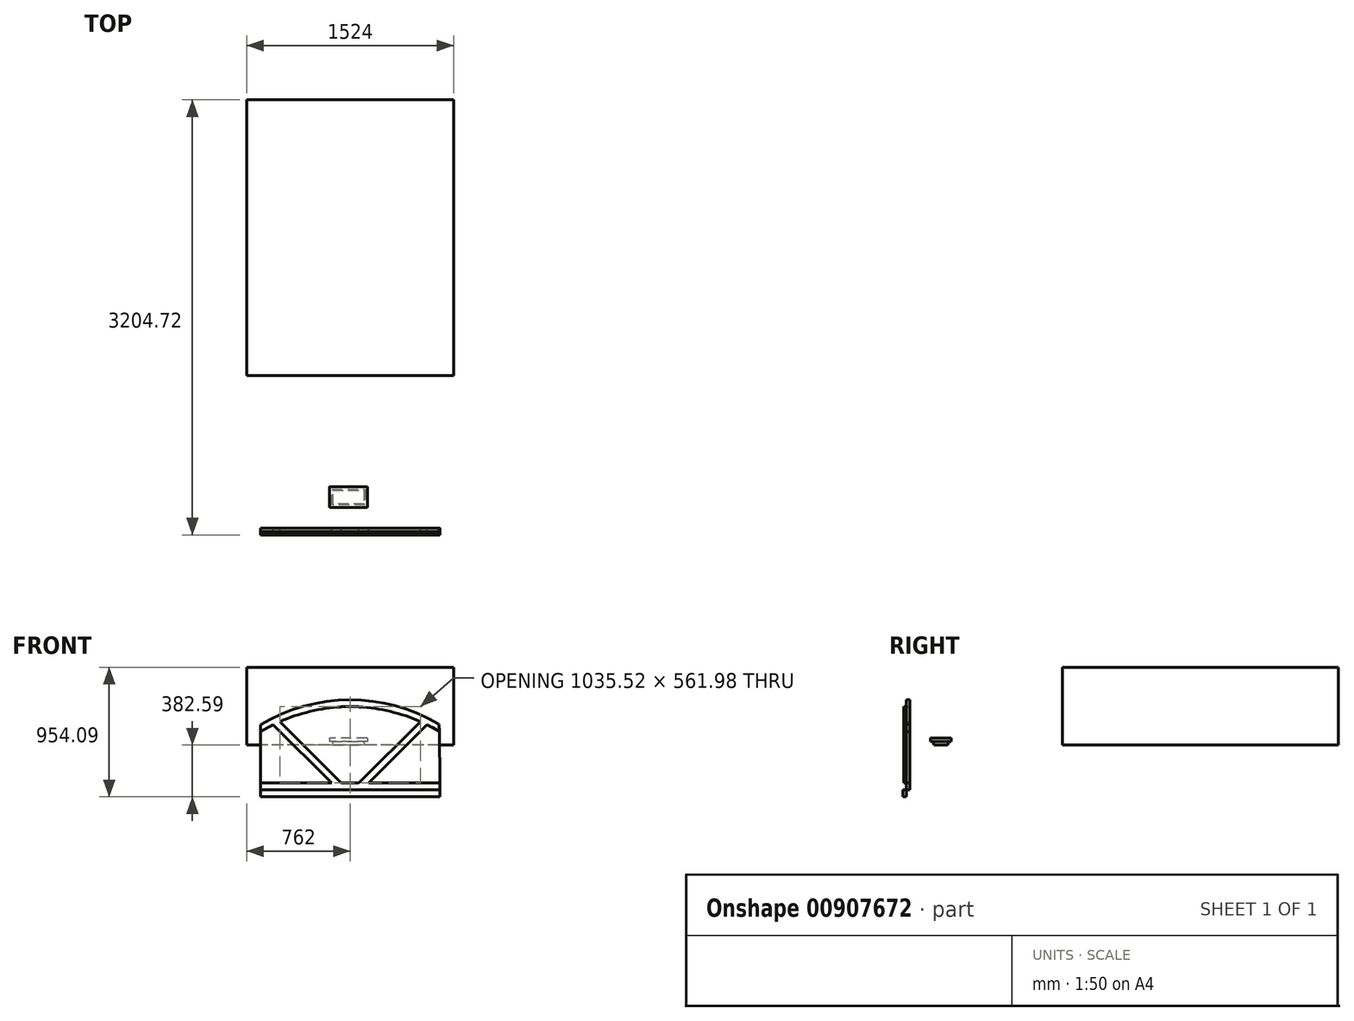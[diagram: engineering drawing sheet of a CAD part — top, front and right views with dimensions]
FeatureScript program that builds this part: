
annotation { "Feature Type Name" : "Feature", "Feature Type Description" : "" }
export const myFeature = defineFeature(function(context is Context, id is Id, definition is map)
    precondition{}
    {
        {
            var Q0;
            Q0=qCreatedBy(makeId("Front.planeOp"),FACE);
            var sketch = newSketch(context, id + "F0", { "sketchPlane" : qUnion([Q0])});
            skLineSegment(sketch, "E0.bottom", {"start": v(65.07, 331.79) * mm, "end": v(-65.07, 331.79) * mm});
            skLineSegment(sketch, "E0.top", {"start": v(660.4, -331.79) * mm, "end": v(-660.4, -331.79) * mm});
            skLineSegment(sketch, "E0.left", {"start": v(660.4, -280.99) * mm, "end": v(660.4, -331.79) * mm});
            skLineSegment(sketch, "E0.right", {"start": v(-660.4, 148.46) * mm, "end": v(-660.4, 97.66) * mm});
            skPoint(sketch, "E0.middle", {"position": v(0, 0) * mm});
            skLineSegment(sketch, "E1", {"start": v(92.3, -280.99) * mm, "end": v(660.4, -280.99) * mm});
            skLineSegment(sketch, "E2", {"start": v(660.4, -280.99) * mm, "end": v(-660.4, -280.99) * mm});
            skLineSegment(sketch, "E3.bottom", {"start": v(-660.4, -280.99) * mm, "end": v(-65.07, -280.99) * mm});
            skLineSegment(sketch, "E3.left", {"start": v(-660.4, 97.66) * mm, "end": v(-660.4, 148.46) * mm});
            skLineSegment(sketch, "E3.right", {"start": v(-65.07, 279.33) * mm, "end": v(-65.07, 280.99) * mm});
            skLineSegment(sketch, "E4.bottom", {"start": v(660.4, -280.99) * mm, "end": v(65.07, -280.99) * mm});
            skLineSegment(sketch, "E4.right", {"start": v(65.07, 279.33) * mm, "end": v(65.07, 280.99) * mm});
            skPoint(sketch, "E5.endSnap0", {"position": v(0, -331.79) * mm});
            skArc(sketch, "E6", {"start": v(660.4, -308.78) * mm, "mid": v(660.25, -294.88) * mm, "end": v(659.82, -280.99) * mm});
            skPoint(sketch, "E5.start.orphan", {"position": v(0, 331.79) * mm});
            skArc(sketch, "E7.trimOffspring", {"start": v(-659.82, -280.99) * mm, "mid": v(-660.22, -293.24) * mm, "end": v(-660.4, -305.5) * mm});
            skArc(sketch, "E8", {"start": v(0, 331.79) * mm, "mid": v(339.27, 286.05) * mm, "end": v(654.31, 152.1) * mm});
            skLineSegment(sketch, "E9", {"start": v(0, -949.34) * mm, "end": v(0, -1000.14) * mm});
            skLineSegment(sketch, "E10.bottom", {"start": v(65.07, 280.99) * mm, "end": v(-65.07, 280.99) * mm});
            skLineSegment(sketch, "E10.left", {"start": v(65.07, 330.13) * mm, "end": v(65.07, 331.79) * mm});
            skLineSegment(sketch, "E10.right", {"start": v(-65.07, 330.13) * mm, "end": v(-65.07, 331.79) * mm});
            skArc(sketch, "E11", {"start": v(0, 331.79) * mm, "mid": v(-342.69, 285.1) * mm, "end": v(-660.4, 148.46) * mm});
            skArc(sketch, "E12", {"start": v(0, 280.99) * mm, "mid": v(341, 234.77) * mm, "end": v(657.4, 99.46) * mm});
            skArc(sketch, "E13", {"start": v(0, 280.99) * mm, "mid": v(-342.69, 234.3) * mm, "end": v(-660.4, 97.66) * mm});
            skLineSegment(sketch, "E14", {"start": v(65.07, -280.99) * mm, "end": v(517.76, 171.7) * mm});
            skLineSegment(sketch, "E15", {"start": v(-65.07, -280.99) * mm, "end": v(-517.76, 171.7) * mm});
            skLineSegment(sketch, "E16", {"start": v(327.34, -90.56) * mm, "end": v(566.72, 148.82) * mm});
            skLineSegment(sketch, "E17", {"start": v(566.72, 148.82) * mm, "end": v(136.92, -280.99) * mm});
            skLineSegment(sketch, "E18", {"start": v(-327.34, -90.56) * mm, "end": v(-136.92, -280.99) * mm});
            skLineSegment(sketch, "E19", {"start": v(-136.92, -280.99) * mm, "end": v(-566.72, 148.82) * mm});
            skPoint(sketch, "E20.start.orphan", {"position": v(291.42, -54.64) * mm});
            skPoint(sketch, "E21.start.orphan", {"position": v(-291.42, -54.64) * mm});
            skPoint(sketch, "E22.orphan", {"position": v(65.07, 382.59) * mm});
            skPoint(sketch, "E23.orphan", {"position": v(-65.07, 382.59) * mm});
            skPoint(sketch, "E24.orphan", {"position": v(660.4, 331.79) * mm});
            skLineSegment(sketch, "E25.trimOffspring", {"start": v(-660.4, -280.99) * mm, "end": v(-660.4, -331.79) * mm});
            skPoint(sketch, "E26.orphan", {"position": v(-660.4, 331.79) * mm});
            skLineSegment(sketch, "E27", {"start": v(657.4, 99.46) * mm, "end": v(654.31, 152.1) * mm});
            skSolve(sketch);
        }
        {
            var Q0;
            {var subQ0=sQuery(id+"F0.wireOp",EDGE,"E15");Q0=makeQuery(id+"F0.imprint","IMPRINT",FACE,{"disambiguationData":[TD([[makeQuery(id+"F0.imprint","IMPRINT",EDGE,{"derivedFrom":subQ0}),1.0]])]});}
            var Q1;
            {var subQ9=sQuery(id+"F0.wireOp",EDGE,"E0.top");Q1=makeQuery(id+"F0.imprint","IMPRINT",FACE,{"disambiguationData":[TD([[makeQuery(id+"F0.imprint","IMPRINT",EDGE,{"derivedFrom":subQ9}),-1.0]])]});}
            var Q2;
            {var subQ0=sQuery(id+"F0.wireOp",EDGE,"E14");Q2=makeQuery(id+"F0.imprint","IMPRINT",FACE,{"disambiguationData":[TD([[makeQuery(id+"F0.imprint","IMPRINT",EDGE,{"derivedFrom":subQ0}),-1.0]])]});}
            var Q3;
            {var subQ8=sQuery(id+"F0.wireOp",EDGE,"E3.right");Q3=makeQuery(id+"F0.imprint","IMPRINT",FACE,{"disambiguationData":[TD([[makeQuery(id+"F0.imprint","IMPRINT",EDGE,{"derivedFrom":subQ8}),1.0]])]});}
            extrude(context, id + "F1", {"entities" : qUnion([Q0, Q1, Q2, Q3]), "depth" : 25.4 * mm, "offsetDistance" : 25.4 * mm});
        }
        {
            var Q0;
            Q0=makeQuery(id+"F1.opExtrude","CAP_FACE",FACE,{"disambiguationData":[OSD([sQuery(id+"F0.wireOp",EDGE,"E0.top"),sQuery(id+"F0.wireOp",EDGE,"E0.left"),sQuery(id+"F0.wireOp",EDGE,"E2"),sQuery(id+"F0.wireOp",EDGE,"E3.bottom"),sQuery(id+"F0.wireOp",EDGE,"E3.right"),sQuery(id+"F0.wireOp",EDGE,"E4.bottom"),sQuery(id+"F0.wireOp",EDGE,"E4.right"),sQuery(id+"F0.wireOp",EDGE,"E6"),sQuery(id+"F0.wireOp",EDGE,"E8"),sQuery(id+"F0.wireOp",EDGE,"E10.bottom"),sQuery(id+"F0.wireOp",EDGE,"E11"),sQuery(id+"F0.wireOp",EDGE,"E12"),sQuery(id+"F0.wireOp",EDGE,"E13"),sQuery(id+"F0.wireOp",EDGE,"E14"),sQuery(id+"F0.wireOp",EDGE,"E15"),sQuery(id+"F0.wireOp",EDGE,"E17"),sQuery(id+"F0.wireOp",EDGE,"E19"),sQuery(id+"F0.wireOp",EDGE,"E25.trimOffspring"),sQuery(id+"F0.wireOp",EDGE,"E0.right"),sQuery(id+"F0.wireOp",EDGE,"E27")])],"isStart":false});
            var sketch = newSketch(context, id + "F2", { "sketchPlane" : qUnion([Q0])});
            skLineSegment(sketch, "E28.bottom", {"start": v(-660.4, -331.79) * mm, "end": v(660.4, -331.79) * mm});
            skLineSegment(sketch, "E28.top", {"start": v(-660.4, -382.59) * mm, "end": v(660.4, -382.59) * mm});
            skLineSegment(sketch, "E28.left", {"start": v(-660.4, -331.79) * mm, "end": v(-660.4, -382.59) * mm});
            skLineSegment(sketch, "E28.right", {"start": v(660.4, -331.79) * mm, "end": v(660.4, -382.59) * mm});
            skSolve(sketch);
        }
        {
            var Q0;
            Q0=makeQuery(id+"F2.imprint","IMPRINT",FACE,{"disambiguationData":[TD([[makeQuery(id+"F2.imprint","IMPRINT",EDGE,{"derivedFrom":sQuery(id+"F2.wireOp",EDGE,"E28.bottom")}),1.0]])]});
            extrude(context, id + "F3", {"entities" : qUnion([Q0]), "depth" : 25.4 * mm, "offsetDistance" : 25.4 * mm});
        }
        {
            var Q0;
            Q0=qCreatedBy(makeId("Top.planeOp"),FACE);
            var sketch = newSketch(context, id + "F4", { "sketchPlane" : qUnion([Q0])});
            skLineSegment(sketch, "E29.bottom", {"start": v(101.76, 278.3) * mm, "end": v(-126.84, 278.3) * mm});
            skLineSegment(sketch, "E29.top", {"start": v(101.76, 176.7) * mm, "end": v(-126.84, 176.7) * mm});
            skLineSegment(sketch, "E29.left", {"start": v(101.76, 278.3) * mm, "end": v(101.76, 176.7) * mm});
            skLineSegment(sketch, "E29.right", {"start": v(-126.84, 278.3) * mm, "end": v(-126.84, 176.7) * mm});
            skPoint(sketch, "E29.middle", {"position": v(-12.54, 227.5) * mm});
            skSolve(sketch);
        }
        {
            var Q0;
            Q0=makeQuery(id+"F4.imprint","IMPRINT",FACE,{"disambiguationData":[TD([[makeQuery(id+"F4.imprint","IMPRINT",EDGE,{"derivedFrom":sQuery(id+"F4.wireOp",EDGE,"E29.bottom")}),1.0]])]});
            extrude(context, id + "F5", {"entities" : qUnion([Q0]), "depth" : 25.4 * mm, "offsetDistance" : 25.4 * mm, "hasDraft" : true, "draftAngle" : 15 * degree});
        }
        {
            var Q0;
            Q0=makeQuery(id+"F5.opExtrude","CAP_FACE",FACE,{"disambiguationData":[OSD([sQuery(id+"F4.wireOp",EDGE,"E29.bottom"),sQuery(id+"F4.wireOp",EDGE,"E29.top"),sQuery(id+"F4.wireOp",EDGE,"E29.left"),sQuery(id+"F4.wireOp",EDGE,"E29.right")])],"isStart":false});
            var sketch = newSketch(context, id + "F6", { "sketchPlane" : qUnion([Q0])});
            skLineSegment(sketch, "E30.bottom", {"start": v(127.16, 303.7) * mm, "end": v(-152.24, 303.7) * mm});
            skLineSegment(sketch, "E30.top", {"start": v(127.16, 151.3) * mm, "end": v(-152.24, 151.3) * mm});
            skLineSegment(sketch, "E30.left", {"start": v(127.16, 303.7) * mm, "end": v(127.16, 151.3) * mm});
            skLineSegment(sketch, "E30.right", {"start": v(-152.24, 303.7) * mm, "end": v(-152.24, 151.3) * mm});
            skPoint(sketch, "E30.middle", {"position": v(-12.54, 227.5) * mm});
            skPoint(sketch, "E30.middle.positionSnap0", {"position": v(-133.65, 227.5) * mm});
            skPoint(sketch, "E30.middle.positionSnap1", {"position": v(-12.54, 285.1) * mm});
            skPoint(sketch, "E30.centerSnap0", {"position": v(-133.65, 227.5) * mm});
            skPoint(sketch, "E30.centerSnap1", {"position": v(-12.54, 285.1) * mm});
            skSolve(sketch);
        }
        {
            var Q0;
            Q0=makeQuery(id+"F6.imprint","IMPRINT",FACE,{"disambiguationData":[TD([[makeQuery(id+"F6.imprint","IMPRINT",EDGE,{"derivedFrom":sQuery(id+"F6.wireOp",EDGE,"E30.bottom")}),1.0]])]});
            var Q1;
            Q1=makeQuery(id+"F6.imprint","IMPRINT",FACE,{"disambiguationData":[TD([[makeQuery(id+"F6.imprint","IMPRINT",EDGE,{"derivedFrom":makeQuery(id+"F5.opExtrude","CAP_EDGE",EDGE,{"disambiguationData":[OSD([sQuery(id+"F4.wireOp",EDGE,"E29.bottom")])],"isStart":false})}),1.0]])]});
            extrude(context, id + "F7", {"entities" : qUnion([Q0, Q1]), "operationType" : NewBodyOperationType.ADD, "depth" : 25.4 * mm, "offsetDistance" : 25.4 * mm});
        }
        {
            var Q0;
            Q0=makeQuery(id+"F7.opExtrude","CAP_EDGE",EDGE,{"disambiguationData":[OSD([sQuery(id+"F6.wireOp",EDGE,"E30.left")])],"isStart":false});
            var Q1;
            Q1=makeQuery(id+"F7.opExtrude","CAP_EDGE",EDGE,{"disambiguationData":[OSD([sQuery(id+"F6.wireOp",EDGE,"E30.top")])],"isStart":false});
            var Q2;
            Q2=makeQuery(id+"F7.opExtrude","CAP_EDGE",EDGE,{"disambiguationData":[OSD([sQuery(id+"F6.wireOp",EDGE,"E30.bottom")])],"isStart":false});
            var Q3;
            Q3=makeQuery(id+"F7.opExtrude","CAP_EDGE",EDGE,{"disambiguationData":[OSD([sQuery(id+"F6.wireOp",EDGE,"E30.right")])],"isStart":false});
            fillet(context, id + "F8", {"entities" : qUnion([Q0, Q1, Q2, Q3]), "radius" : 5.08 * mm, "tangentPropagation" : true, "allowEdgeOverflow" : false});
        }
        {
            var Q0;
            Q0=qCreatedBy(makeId("Top.planeOp"),FACE);
            var sketch = newSketch(context, id + "F9", { "sketchPlane" : qUnion([Q0])});
            skLineSegment(sketch, "E31.bottom", {"start": v(762, 1121.92) * mm, "end": v(-762, 1121.92) * mm});
            skLineSegment(sketch, "E31.top", {"start": v(762, 3153.92) * mm, "end": v(-762, 3153.92) * mm});
            skLineSegment(sketch, "E31.left", {"start": v(762, 1121.92) * mm, "end": v(762, 3153.92) * mm});
            skLineSegment(sketch, "E31.right", {"start": v(-762, 1121.92) * mm, "end": v(-762, 3153.92) * mm});
            skPoint(sketch, "E31.middle", {"position": v(0, 2137.92) * mm});
            skSolve(sketch);
        }
        {
            var Q0;
            Q0=makeQuery(id+"F9.imprint","IMPRINT",FACE,{"disambiguationData":[TD([[makeQuery(id+"F9.imprint","IMPRINT",EDGE,{"derivedFrom":sQuery(id+"F9.wireOp",EDGE,"E31.bottom")}),-1.0]])]});
            extrude(context, id + "F10", {"entities" : qUnion([Q0]), "depth" : 571.5 * mm, "offsetDistance" : 25.4 * mm});
        }
        {
            var Q0;
            Q0=makeQuery(id+"F1.opExtrude","CAP_FACE",FACE,{"disambiguationData":[OSD([sQuery(id+"F0.wireOp",EDGE,"E0.top"),sQuery(id+"F0.wireOp",EDGE,"E0.left"),sQuery(id+"F0.wireOp",EDGE,"E2"),sQuery(id+"F0.wireOp",EDGE,"E3.bottom"),sQuery(id+"F0.wireOp",EDGE,"E3.right"),sQuery(id+"F0.wireOp",EDGE,"E4.bottom"),sQuery(id+"F0.wireOp",EDGE,"E4.right"),sQuery(id+"F0.wireOp",EDGE,"E6"),sQuery(id+"F0.wireOp",EDGE,"E8"),sQuery(id+"F0.wireOp",EDGE,"E10.bottom"),sQuery(id+"F0.wireOp",EDGE,"E11"),sQuery(id+"F0.wireOp",EDGE,"E12"),sQuery(id+"F0.wireOp",EDGE,"E13"),sQuery(id+"F0.wireOp",EDGE,"E14"),sQuery(id+"F0.wireOp",EDGE,"E15"),sQuery(id+"F0.wireOp",EDGE,"E17"),sQuery(id+"F0.wireOp",EDGE,"E19"),sQuery(id+"F0.wireOp",EDGE,"E25.trimOffspring"),sQuery(id+"F0.wireOp",EDGE,"E0.right"),sQuery(id+"F0.wireOp",EDGE,"E27")])],"isStart":false});
            var sketch = newSketch(context, id + "F11", { "sketchPlane" : qUnion([Q0])});
            skLineSegment(sketch, "E32", {"start": v(657.4, 99.46) * mm, "end": v(566.72, 148.82) * mm});
            skLineSegment(sketch, "E33", {"start": v(566.72, 148.82) * mm, "end": v(136.92, -280.99) * mm});
            skLineSegment(sketch, "E34", {"start": v(136.92, -280.99) * mm, "end": v(659.82, -280.99) * mm});
            skLineSegment(sketch, "E35", {"start": v(659.82, -280.99) * mm, "end": v(657.4, 99.46) * mm});
            skLineSegment(sketch, "E36", {"start": v(517.76, 171.7) * mm, "end": v(65.07, -280.99) * mm});
            skLineSegment(sketch, "E37", {"start": v(65.07, -280.99) * mm, "end": v(-65.07, -280.99) * mm});
            skLineSegment(sketch, "E38", {"start": v(-65.07, -280.99) * mm, "end": v(-517.76, 171.7) * mm});
            skLineSegment(sketch, "E39", {"start": v(-660.4, 97.66) * mm, "end": v(-566.72, 148.82) * mm});
            skLineSegment(sketch, "E40", {"start": v(-566.72, 148.82) * mm, "end": v(-136.92, -280.99) * mm});
            skLineSegment(sketch, "E41", {"start": v(-136.92, -280.99) * mm, "end": v(-660.4, -280.99) * mm});
            skLineSegment(sketch, "E42", {"start": v(-660.4, -280.99) * mm, "end": v(-660.4, 97.66) * mm});
            skArc(sketch, "E43", {"start": v(517.76, 171.7) * mm, "mid": v(0, 282.66) * mm, "end": v(-517.76, 171.7) * mm});
            skSolve(sketch);
        }
        {
            var Q0;
            Q0=makeQuery(id+"F11.imprint","IMPRINT",FACE,{"disambiguationData":[TD([[makeQuery(id+"F11.imprint","IMPRINT",EDGE,{"derivedFrom":sQuery(id+"F11.wireOp",EDGE,"E32")}),1.0]])]});
            var Q1;
            Q1=makeQuery(id+"F11.imprint","IMPRINT",FACE,{"disambiguationData":[TD([[makeQuery(id+"F11.imprint","IMPRINT",EDGE,{"derivedFrom":sQuery(id+"F11.wireOp",EDGE,"E36")}),1.0]])]});
            var Q2;
            Q2=makeQuery(id+"F11.imprint","IMPRINT",FACE,{"disambiguationData":[TD([[makeQuery(id+"F11.imprint","IMPRINT",EDGE,{"derivedFrom":sQuery(id+"F11.wireOp",EDGE,"E39")}),-1.0]])]});
            extrude(context, id + "F12", {"entities" : qUnion([Q0, Q1, Q2]), "depth" : 19.05 * mm, "offsetDistance" : 25.4 * mm});
        }
    });
